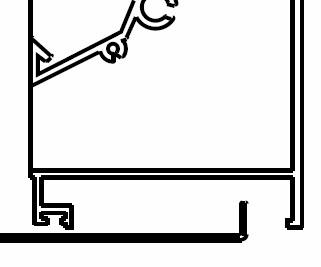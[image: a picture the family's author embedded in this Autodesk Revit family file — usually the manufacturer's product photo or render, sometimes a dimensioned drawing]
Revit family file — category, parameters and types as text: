
# Revit family: Louver_Carnes-Ext_Alum-Drainable-Stationary-FPBB
name_source: partatom
category: Duct Accessories
revit_build: Autodesk Revit MEP 2012 (Build: 20110309_2315(x64)
units: mm (PartAtom-declared; Revit-internal decimal feet)

## types (1)
- Louver_Carnes-Ext_Alum-Drainable-Stationary-FPBB
    04 CSI = 08 91 00
    95 CSI = 10200
    Actual Height = 24"
    Actual Width = 24"
    Assembly Code = B2010300
    Blade Material = Metal - Carnes - Steel - Galvanized
    Blade Width = 22 39/128"
    Catalog URL = http://www.carnes.com
    Default Elevation = 0"
    Depth = 4 41/256"
    Description = Extruded Aluminum Stationary Drainable Blade Louver
    Duct Connector 1 = Duct Connection 1
    Duct Connector 2 = Duct Connection 2
    Frame Material = Metal - Carnes - Steel - Galvanized
    Height = 24"
    Manufacturer = CARNES COMPANY
    Manufacturer Fax = 608-845-6470
    Maximum Horinzontal Size = 120"W x 84"H
    Maximum System Pressure = 0.70 in-wg
    Maximum System Velocity = 1250 FPM
    Maximum Vertical Size = 84"W x 120"H
    Minimum Size = 12"W x 12"H
    Model = FPBB
    Offset = 3"
    Product Line = Extruded Aluminum Stationary Drainable Blade Louver
    Product Page URL = http://www.carnes.com
    Spec Sheet URL = http://www.carnes.com
    Subcategory = Louvers and Dampers
    URL = http://www.carnes.com
    Warranty URL = http://www.carnes.com
    Width = 24"
    ecoScorecard Product Page = http://ecoscorecard.com

## geometry (parser evidence)
native form markers: Sweep x7
no freeform markers — native parametric forms only
